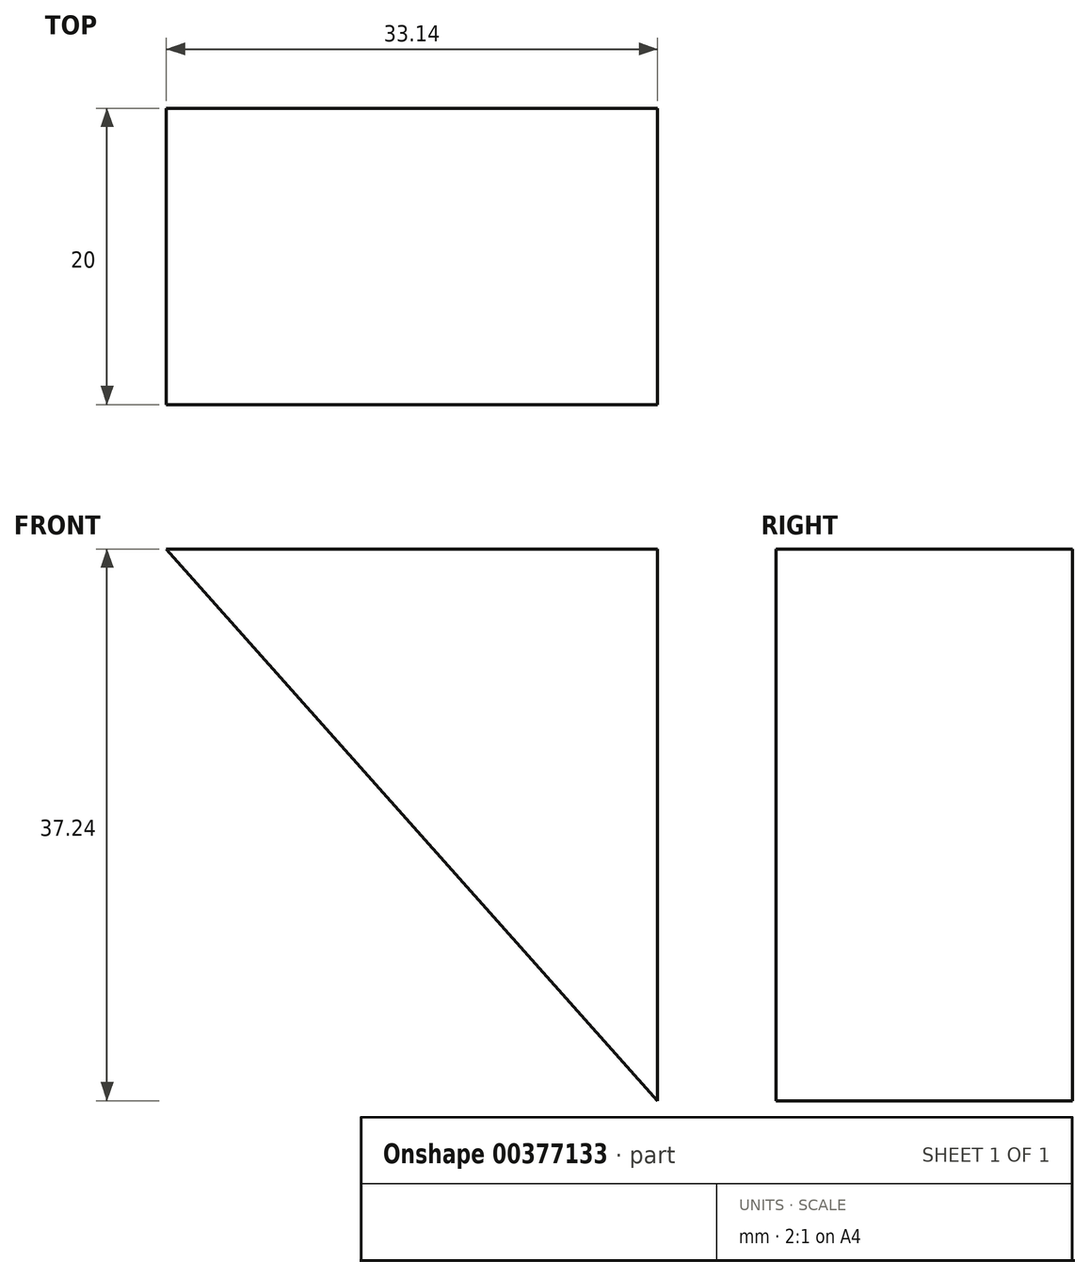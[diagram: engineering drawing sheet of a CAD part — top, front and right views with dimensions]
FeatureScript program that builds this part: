
annotation { "Feature Type Name" : "Feature", "Feature Type Description" : "" }
export const myFeature = defineFeature(function(context is Context, id is Id, definition is map)
    precondition{}
    {
        {
            var Q0;
            Q0=qCreatedBy(makeId("Front.planeOp"),FACE);
            var sketch = newSketch(context, id + "F0", { "sketchPlane" : qUnion([Q0])});
            skLineSegment(sketch, "E0", {"start": v(-48.05, 55.76) * mm, "end": v(-14.91, 55.76) * mm});
            skLineSegment(sketch, "E1", {"start": v(-14.91, 55.76) * mm, "end": v(-14.91, 18.52) * mm});
            skLineSegment(sketch, "E2", {"start": v(-14.91, 18.52) * mm, "end": v(-48.05, 55.76) * mm});
            skSolve(sketch);
        }
        {
            var Q0;
            Q0 = qSketchRegion(id + "F0", true);
            extrude(context, id + "F1", {"entities" : qUnion([Q0]), "depth" : 20 * mm});
        }
    });
